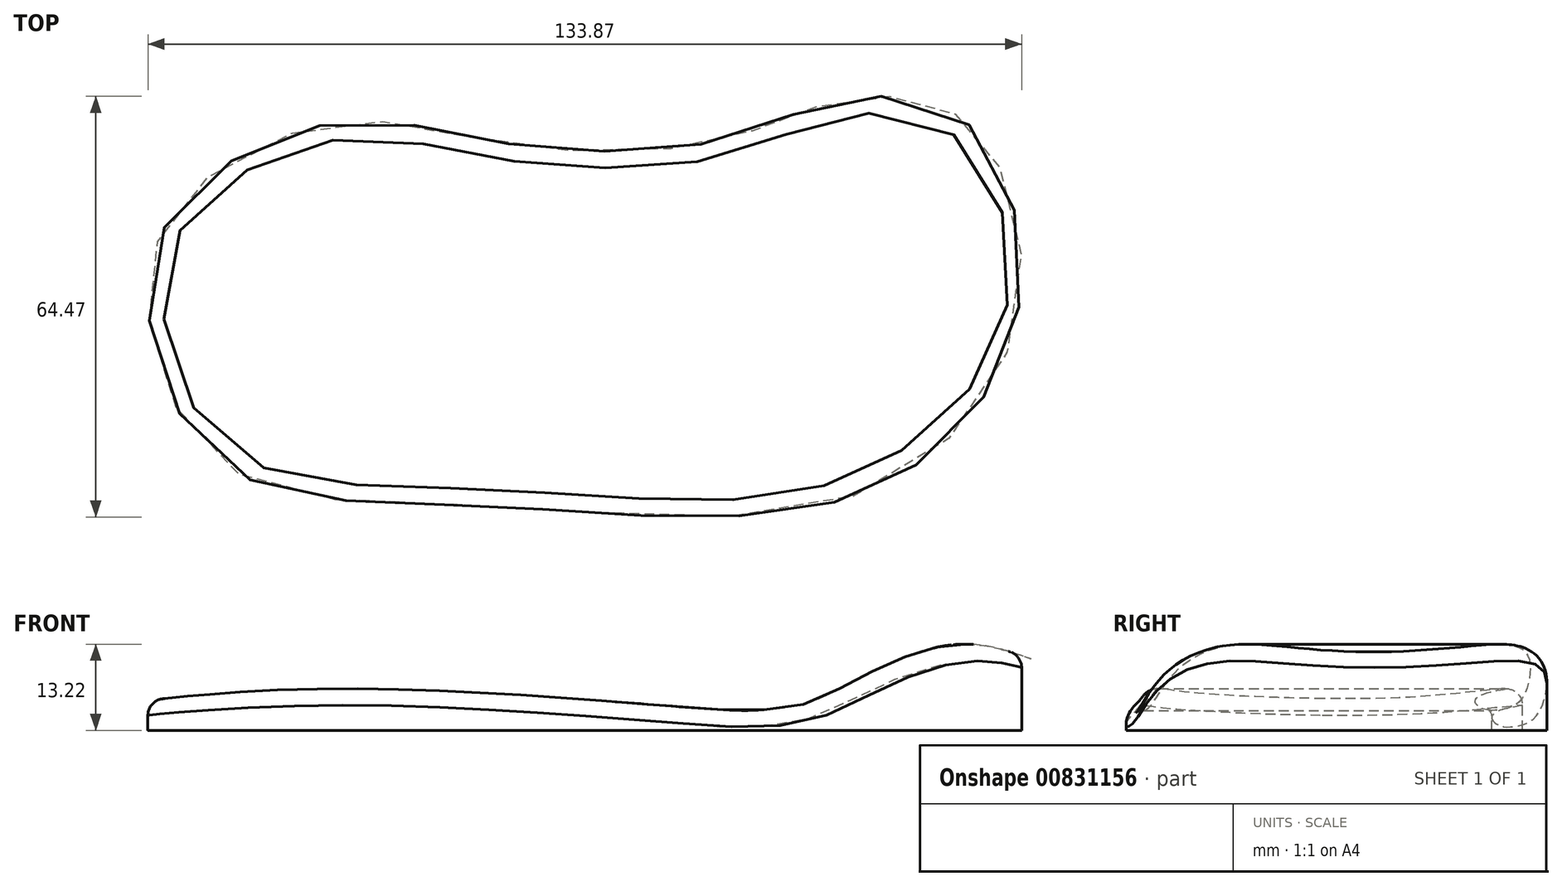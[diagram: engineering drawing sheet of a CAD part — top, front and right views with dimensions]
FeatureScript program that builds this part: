
annotation { "Feature Type Name" : "Feature", "Feature Type Description" : "" }
export const myFeature = defineFeature(function(context is Context, id is Id, definition is map)
    precondition{}
    {
        {
            var Q0;
            Q0=qCreatedBy(makeId("Top.planeOp"),FACE);
            var sketch = newSketch(context, id + "F0", { "sketchPlane" : qUnion([Q0])});
            skFitSpline(sketch, "E0", {"points": [v(-64, 0) * mm, v(-58.72, 18.6) * mm, v(-34.17, 30.48) * mm, v(-8.58, 27.05) * mm, v(23.1, 27.58) * mm, v(38.4, 32.86) * mm, v(55.02, 33.65) * mm, v(65.84, 24.41) * mm, v(68.22, -2.5) * mm, v(43.41, -27.05) * mm, v(-12.8, -28.37) * mm, v(-51.86, -22.56) * mm, v(-64, 0) * mm]});
            skSolve(sketch);
        }
        {
            var Q0;
            Q0=qCreatedBy(makeId("Front.planeOp"),FACE);
            var sketch = newSketch(context, id + "F1", { "sketchPlane" : qUnion([Q0])});
            skFitSpline(sketch, "E1", {"points": [v(-78.24, 2.86) * mm, v(-30.62, 6.4) * mm, v(24.36, 3.13) * mm, v(29.26, 3.13) * mm, v(36.06, 3.95) * mm, v(44.77, 8.03) * mm, v(60, 13.2) * mm, v(74.16, 9.66) * mm], "startDerivative": vector(186.27, 24.44) * mm, "endDerivative": vector(108.33, -44.77) * mm});
            skSolve(sketch);
        }
        {
            var Q0;
            Q0 = qSketchRegion(id + "F1", true);
            var Q1;
            Q1 = qConstructionFilter(qBodyType(qCreatedBy(id + "F1" ,EDGE), BodyType.WIRE), ConstructionObject.NO);
            extrude(context, id + "F2", {"entities" : qUnion([Q0]), "bodyType" : ToolBodyType.SURFACE, "surfaceEntities" : qUnion([Q1]), "endBound" : BoundingType.SYMMETRIC, "depth" : 76.2 * mm, "offsetDistance" : 25.4 * mm});
        }
        {
            var Q0;
            Q0 = qSketchRegion(id + "F0", true);
            var Q1;
            Q1=makeQuery(id+"F2.opExtrude","SWEPT_FACE",FACE,{"disambiguationData":[OSD([sQuery(id+"F1.wireOp",EDGE,"E1")])]});
            extrude(context, id + "F3", {"entities" : qUnion([Q0]), "endBound" : BoundingType.UP_TO_SURFACE, "depth" : 25.4 * mm, "endBoundEntityFace" : qUnion([Q1]), "offsetDistance" : 25.4 * mm});
        }
        {
            var Q0;
            Q0=makeQuery(id+"F3.opExtrude","CAP_EDGE",EDGE,{"disambiguationData":[OSD([sQuery(id+"F0.wireOp",EDGE,"E0")])],"isStart":false});
            fillet(context, id + "F4", {"entities" : qUnion([Q0]), "radius" : 2.54 * mm, "tangentPropagation" : true, "allowEdgeOverflow" : false});
        }
    });
